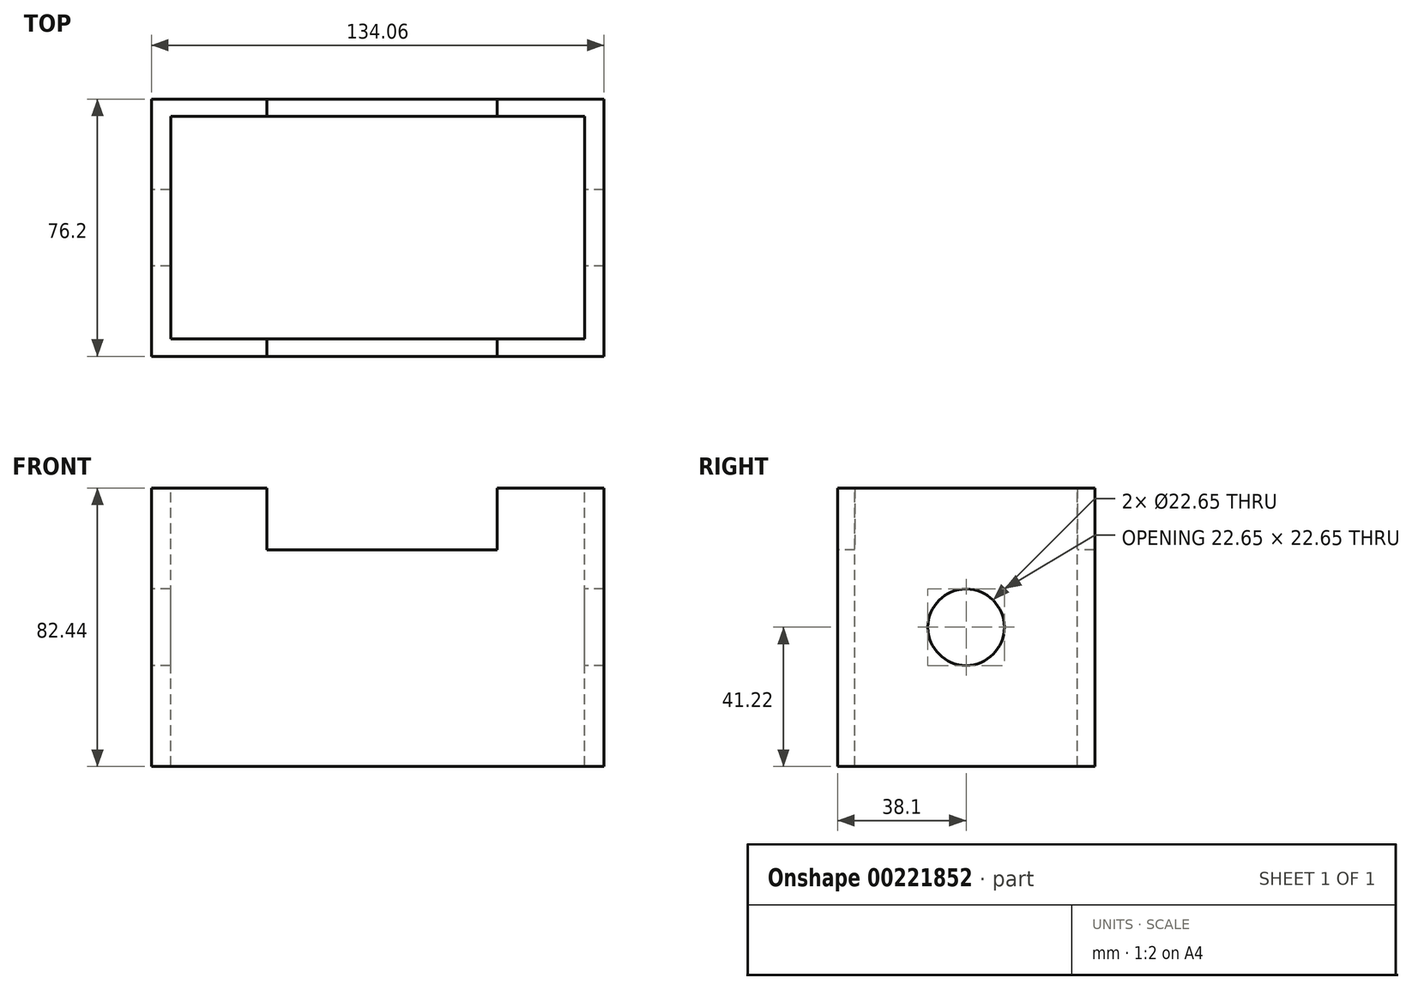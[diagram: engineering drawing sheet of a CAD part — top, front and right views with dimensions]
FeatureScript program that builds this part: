
annotation { "Feature Type Name" : "Feature", "Feature Type Description" : "" }
export const myFeature = defineFeature(function(context is Context, id is Id, definition is map)
    precondition{}
    {
        {
            var Q0;
            Q0=qCreatedBy(makeId("Front.planeOp"),FACE);
            var sketch = newSketch(context, id + "F0", { "sketchPlane" : qUnion([Q0])});
            skLineSegment(sketch, "E0.bottom", {"start": v(67.03, -41.22) * mm, "end": v(-67.03, -41.22) * mm});
            skLineSegment(sketch, "E0.top", {"start": v(67.03, 41.22) * mm, "end": v(-67.03, 41.22) * mm});
            skLineSegment(sketch, "E0.left", {"start": v(67.03, -41.22) * mm, "end": v(67.03, 41.22) * mm});
            skLineSegment(sketch, "E0.right", {"start": v(-67.03, -41.22) * mm, "end": v(-67.03, 41.22) * mm});
            skPoint(sketch, "E0.middle", {"position": v(0, 0) * mm});
            skSolve(sketch);
        }
        {
            var Q0;
            Q0 = qSketchRegion(id + "F0", true);
            extrude(context, id + "F1", {"entities" : qUnion([Q0]), "depth" : 38.1 * mm, "hasSecondDirection" : true, "secondDirectionOppositeDirection" : true, "secondDirectionDepth" : 38.1 * mm});
        }
        {
            var Q0;
            Q0=qCreatedBy(makeId("Right.planeOp"),FACE);
            var sketch = newSketch(context, id + "F2", { "sketchPlane" : qUnion([Q0])});
            skCircle(sketch, "E1", {"center": v(0, 0) * mm, "radius": 11.32 * mm});
            skSolve(sketch);
        }
        {
            var Q0;
            Q0 = qSketchRegion(id + "F2", true);
            extrude(context, id + "F3", {"entities" : qUnion([Q0]), "operationType" : NewBodyOperationType.REMOVE, "depth" : 93.73 * mm, "hasSecondDirection" : true, "secondDirectionOppositeDirection" : true, "secondDirectionDepth" : 71.37 * mm});
        }
        {
            var Q0;
            Q0=qCreatedBy(makeId("Front.planeOp"),FACE);
            var sketch = newSketch(context, id + "F4", { "sketchPlane" : qUnion([Q0])});
            skLineSegment(sketch, "E2", {"start": v(-83, 22.96) * mm, "end": v(75.59, 22.96) * mm});
            skLineSegment(sketch, "E3.bottom", {"start": v(-32.8, 56.9) * mm, "end": v(35.37, 56.9) * mm});
            skLineSegment(sketch, "E3.top", {"start": v(-32.8, 22.96) * mm, "end": v(35.37, 22.96) * mm});
            skLineSegment(sketch, "E3.left", {"start": v(-32.8, 56.9) * mm, "end": v(-32.8, 22.96) * mm});
            skLineSegment(sketch, "E3.right", {"start": v(35.37, 56.9) * mm, "end": v(35.37, 22.96) * mm});
            skPoint(sketch, "E4.start.orphan", {"position": v(0, 62.33) * mm});
            skSolve(sketch);
        }
        {
            var Q0;
            Q0 = qSketchRegion(id + "F4", true);
            extrude(context, id + "F5", {"entities" : qUnion([Q0]), "operationType" : NewBodyOperationType.REMOVE, "oppositeDirection" : true, "depth" : 44.96 * mm, "hasSecondDirection" : true, "secondDirectionOppositeDirection" : false, "secondDirectionDepth" : 59.69 * mm});
        }
        {
            var Q0;
            Q0=qCreatedBy(makeId("Top.planeOp"),FACE);
            var sketch = newSketch(context, id + "F6", { "sketchPlane" : qUnion([Q0])});
            skLineSegment(sketch, "E5.bottom", {"start": v(61.33, -32.95) * mm, "end": v(-61.33, -32.95) * mm});
            skLineSegment(sketch, "E5.top", {"start": v(61.33, 32.95) * mm, "end": v(-61.33, 32.95) * mm});
            skLineSegment(sketch, "E5.left", {"start": v(61.33, -32.95) * mm, "end": v(61.33, 32.95) * mm});
            skLineSegment(sketch, "E5.right", {"start": v(-61.33, -32.95) * mm, "end": v(-61.33, 32.95) * mm});
            skPoint(sketch, "E5.middle", {"position": v(0, 0) * mm});
            skSolve(sketch);
        }
        {
            var Q0;
            Q0 = qSketchRegion(id + "F6", true);
            extrude(context, id + "F7", {"entities" : qUnion([Q0]), "operationType" : NewBodyOperationType.REMOVE, "oppositeDirection" : true, "depth" : 79.76 * mm, "hasSecondDirection" : true, "secondDirectionOppositeDirection" : false, "secondDirectionDepth" : 65.8 * mm});
        }
    });
